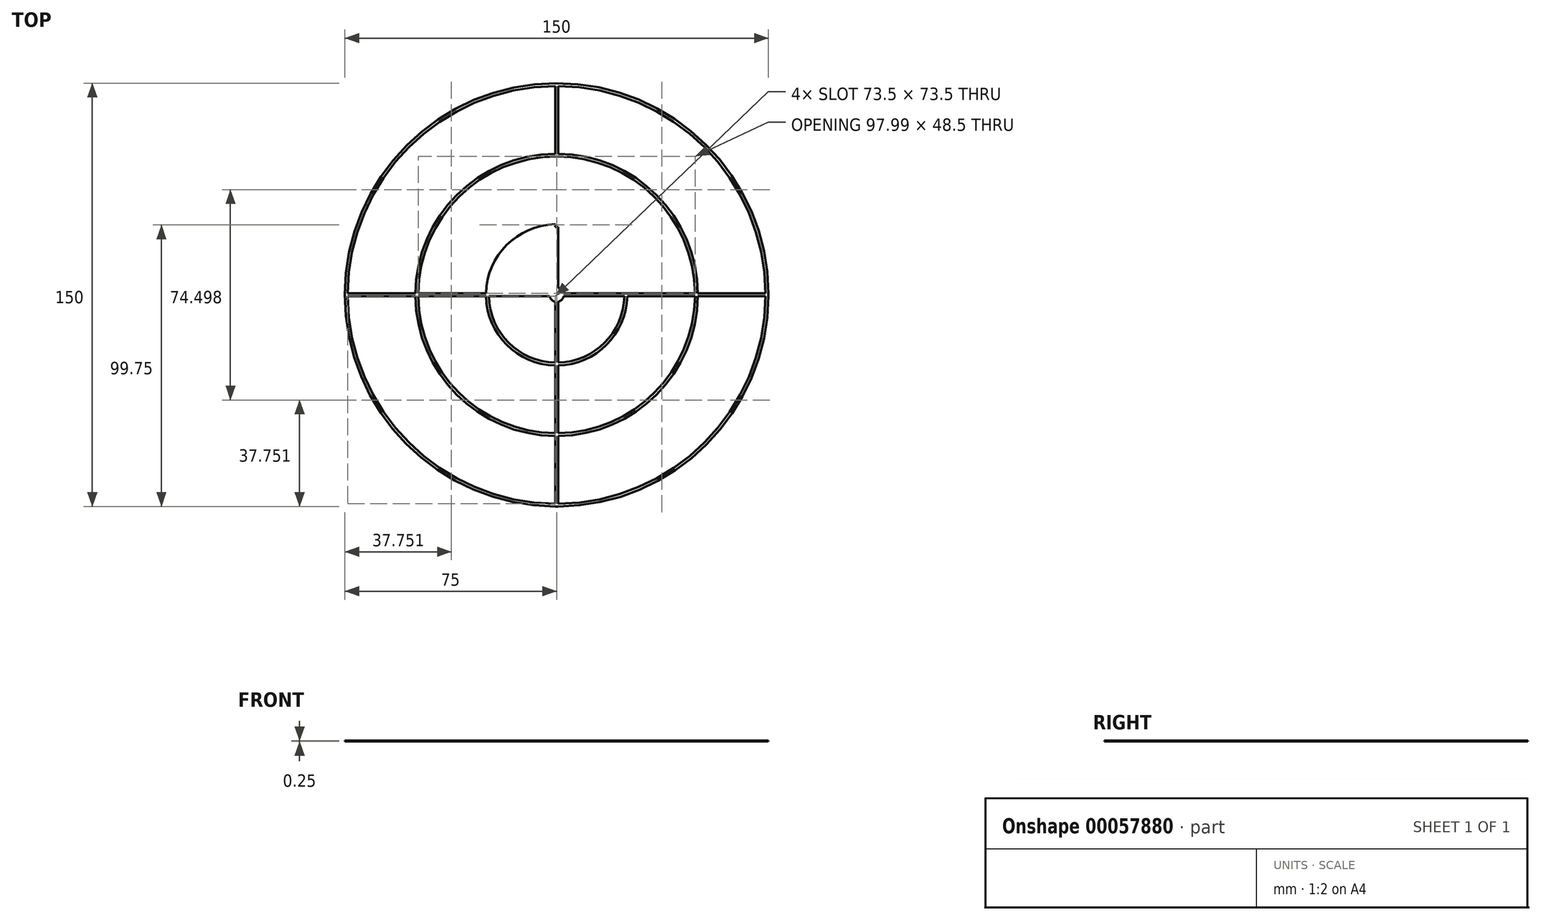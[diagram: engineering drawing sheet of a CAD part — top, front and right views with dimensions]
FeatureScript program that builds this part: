
annotation { "Feature Type Name" : "Feature", "Feature Type Description" : "" }
export const myFeature = defineFeature(function(context is Context, id is Id, definition is map)
    precondition{}
    {
        {
            var Q0;
            Q0=qCreatedBy(makeId("Top.planeOp"),FACE);
            var sketch = newSketch(context, id + "F0", { "sketchPlane" : qUnion([Q0])});
            skArc(sketch, "E0", {"start": v(-74, -0.5) * mm, "mid": v(74, 0) * mm, "end": v(-74, 0.5) * mm});
            skCircle(sketch, "E1", {"center": v(0, 0) * mm, "radius": 75 * mm});
            skLineSegment(sketch, "E2.rect.bottom", {"start": v(0.5, -75) * mm, "end": v(-0.5, -75) * mm});
            skLineSegment(sketch, "E2.rect.top", {"start": v(0.5, 75) * mm, "end": v(-0.5, 75) * mm});
            skLineSegment(sketch, "E2.rect.left", {"start": v(0.5, -75) * mm, "end": v(0.5, -0.5) * mm});
            skLineSegment(sketch, "E2.rect.right", {"start": v(-0.5, -75) * mm, "end": v(-0.5, -50) * mm});
            skLineSegment(sketch, "E3.rect.bottom", {"start": v(75, -0.5) * mm, "end": v(0.5, -0.5) * mm});
            skLineSegment(sketch, "E3.rect.top", {"start": v(75, 0.5) * mm, "end": v(-24, 0.5) * mm});
            skLineSegment(sketch, "E3.rect.left", {"start": v(75, -0.5) * mm, "end": v(75, 0.5) * mm});
            skLineSegment(sketch, "E3.rect.right", {"start": v(-75, -0.5) * mm, "end": v(-75, 0.5) * mm});
            skArc(sketch, "E4", {"start": v(-25, -0.5) * mm, "mid": v(-17.68, -17.68) * mm, "end": v(-0.5, -25) * mm});
            skArc(sketch, "E5", {"start": v(0.5, -24) * mm, "mid": v(16.97, -16.97) * mm, "end": v(24, -0.5) * mm});
            skArc(sketch, "E6", {"start": v(49, -0.5) * mm, "mid": v(0, 49) * mm, "end": v(-49, -0.5) * mm});
            skArc(sketch, "E7", {"start": v(-50, -0.5) * mm, "mid": v(50, 0) * mm, "end": v(-50, 0.5) * mm});
            skArc(sketch, "E8", {"start": v(0.5, -2.45) * mm, "mid": v(1.77, -1.77) * mm, "end": v(2.45, -0.5) * mm});
            skLineSegment(sketch, "E9.trimOffspring", {"start": v(-50, 0.5) * mm, "end": v(-74, 0.5) * mm});
            skLineSegment(sketch, "E10.trimOffspring", {"start": v(-25, 0.5) * mm, "end": v(-49, 0.5) * mm});
            skLineSegment(sketch, "E11.trimOffspring", {"start": v(0.5, 25) * mm, "end": v(0.5, 75) * mm});
            skArc(sketch, "E12.trimOffspring", {"start": v(-0.5, 25) * mm, "mid": v(-17.68, 17.68) * mm, "end": v(-25, 0.5) * mm});
            skLineSegment(sketch, "E13.trimOffspring", {"start": v(-0.5, -49) * mm, "end": v(-0.5, -25) * mm});
            skArc(sketch, "E14.trimOffspring", {"start": v(0.5, -25) * mm, "mid": v(25, 0) * mm, "end": v(0.5, 25) * mm});
            skLineSegment(sketch, "E15.trimOffspring", {"start": v(-0.5, -24) * mm, "end": v(-0.5, 75) * mm});
            skLineSegment(sketch, "E16.trimOffspring", {"start": v(-0.5, -0.5) * mm, "end": v(-74, -0.5) * mm});
            skArc(sketch, "E17.trimOffspring", {"start": v(24, 0.5) * mm, "mid": v(-16.97, 16.97) * mm, "end": v(-0.5, -24) * mm});
            skArc(sketch, "E18.trimOffspring", {"start": v(2.45, 0.5) * mm, "mid": v(1.77, 1.77) * mm, "end": v(0.5, 2.45) * mm});
            skArc(sketch, "E19.trimOffspring", {"start": v(-0.5, 2.45) * mm, "mid": v(-1.77, 1.77) * mm, "end": v(-2.45, 0.5) * mm});
            skArc(sketch, "E20.trimOffspring", {"start": v(-2.45, -0.5) * mm, "mid": v(-1.77, -1.77) * mm, "end": v(-0.5, -2.45) * mm});
            skLineSegment(sketch, "E21.trimOffspring", {"start": v(0.5, 0.5) * mm, "end": v(0.5, 24) * mm});
            skArc(sketch, "E22", {"start": v(-49, -0.5) * mm, "mid": v(0, -49) * mm, "end": v(49, -0.5) * mm});
            skSolve(sketch);
        }
        {
            var Q0;
            {var subQ0=sQuery(id+"F0.wireOp",EDGE,"E2.rect.right");var subQ1=sQuery(id+"F0.wireOp",EDGE,"E0");var subQ2=makeQuery(id+"F0.imprint","INTERSECT",VERTEX,{"derivedFrom":[subQ1,subQ0]});Q0=makeQuery(id+"F0.imprint","IMPRINT",FACE,{"disambiguationData":[TD([[makeQuery(id+"F0.imprint","IMPRINT",EDGE,{"disambiguationData":[TD([[subQ2,-1.0]])],"derivedFrom":subQ1}),1.0]])]});}
            var Q1;
            {var subQ0=sQuery(id+"F0.wireOp",EDGE,"E3.rect.bottom");var subQ1=sQuery(id+"F0.wireOp",EDGE,"E0");var subQ2=makeQuery(id+"F0.imprint","INTERSECT",VERTEX,{"derivedFrom":[subQ1,subQ0]});Q1=makeQuery(id+"F0.imprint","IMPRINT",FACE,{"disambiguationData":[TD([[makeQuery(id+"F0.imprint","IMPRINT",EDGE,{"disambiguationData":[TD([[subQ2,-1.0]])],"derivedFrom":subQ1}),1.0]])]});}
            var Q2;
            {var subQ0=sQuery(id+"F0.wireOp",EDGE,"E11.trimOffspring");var subQ1=sQuery(id+"F0.wireOp",EDGE,"E0");var subQ2=makeQuery(id+"F0.imprint","INTERSECT",VERTEX,{"derivedFrom":[subQ1,subQ0]});Q2=makeQuery(id+"F0.imprint","IMPRINT",FACE,{"disambiguationData":[TD([[makeQuery(id+"F0.imprint","IMPRINT",EDGE,{"disambiguationData":[TD([[subQ2,-1.0]])],"derivedFrom":subQ1}),1.0]])]});}
            var Q3;
            {var subQ0=sQuery(id+"F0.wireOp",EDGE,"E2.rect.right");var subQ1=sQuery(id+"F0.wireOp",EDGE,"E0");var subQ2=makeQuery(id+"F0.imprint","INTERSECT",VERTEX,{"derivedFrom":[subQ1,subQ0]});Q3=makeQuery(id+"F0.imprint","IMPRINT",FACE,{"disambiguationData":[TD([[makeQuery(id+"F0.imprint","IMPRINT",EDGE,{"disambiguationData":[TD([[subQ2,-1.0]])],"derivedFrom":subQ1}),1.0]])]});}
            var Q4;
            {var subQ0=sQuery(id+"F0.wireOp",EDGE,"E3.rect.bottom");var subQ1=sQuery(id+"F0.wireOp",EDGE,"E0");var subQ2=makeQuery(id+"F0.imprint","INTERSECT",VERTEX,{"derivedFrom":[subQ1,subQ0]});Q4=makeQuery(id+"F0.imprint","IMPRINT",FACE,{"disambiguationData":[TD([[makeQuery(id+"F0.imprint","IMPRINT",EDGE,{"disambiguationData":[TD([[subQ2,-1.0]])],"derivedFrom":subQ1}),1.0]])]});}
            var Q5;
            {var subQ0=sQuery(id+"F0.wireOp",EDGE,"E11.trimOffspring");var subQ1=sQuery(id+"F0.wireOp",EDGE,"E0");var subQ2=makeQuery(id+"F0.imprint","INTERSECT",VERTEX,{"derivedFrom":[subQ1,subQ0]});Q5=makeQuery(id+"F0.imprint","IMPRINT",FACE,{"disambiguationData":[TD([[makeQuery(id+"F0.imprint","IMPRINT",EDGE,{"disambiguationData":[TD([[subQ2,-1.0]])],"derivedFrom":subQ1}),1.0]])]});}
            var Q6;
            {var subQ11=sQuery(id+"F0.wireOp",EDGE,"E3.rect.right");Q6=makeQuery(id+"F0.imprint","IMPRINT",FACE,{"disambiguationData":[TD([[makeQuery(id+"F0.imprint","IMPRINT",EDGE,{"derivedFrom":subQ11}),-1.0]])]});}
            var Q7;
            {var subQ0=sQuery(id+"F0.wireOp",EDGE,"E2.rect.top");Q7=makeQuery(id+"F0.imprint","IMPRINT",FACE,{"disambiguationData":[TD([[makeQuery(id+"F0.imprint","IMPRINT",EDGE,{"derivedFrom":subQ0}),-1.0]])]});}
            var Q8;
            {var subQ0=sQuery(id+"F0.wireOp",EDGE,"E3.rect.right");Q8=makeQuery(id+"F0.imprint","IMPRINT",FACE,{"disambiguationData":[TD([[makeQuery(id+"F0.imprint","IMPRINT",EDGE,{"derivedFrom":subQ0}),1.0]])]});}
            var Q9;
            {var subQ3=sQuery(id+"F0.wireOp",EDGE,"E20.trimOffspring");Q9=makeQuery(id+"F0.imprint","IMPRINT",FACE,{"disambiguationData":[TD([[makeQuery(id+"F0.imprint","IMPRINT",EDGE,{"derivedFrom":subQ3}),1.0]])]});}
            var Q10;
            {var subQ0=sQuery(id+"F0.wireOp",EDGE,"E19.trimOffspring");Q10=makeQuery(id+"F0.imprint","IMPRINT",FACE,{"disambiguationData":[TD([[makeQuery(id+"F0.imprint","IMPRINT",EDGE,{"derivedFrom":subQ0}),1.0]])]});}
            var Q11;
            {var subQ0=sQuery(id+"F0.wireOp",EDGE,"E18.trimOffspring");Q11=makeQuery(id+"F0.imprint","IMPRINT",FACE,{"disambiguationData":[TD([[makeQuery(id+"F0.imprint","IMPRINT",EDGE,{"derivedFrom":subQ0}),1.0]])]});}
            var Q12;
            {var subQ3=sQuery(id+"F0.wireOp",EDGE,"E8");Q12=makeQuery(id+"F0.imprint","IMPRINT",FACE,{"disambiguationData":[TD([[makeQuery(id+"F0.imprint","IMPRINT",EDGE,{"derivedFrom":subQ3}),1.0]])]});}
            var Q13;
            {var subQ4=sQuery(id+"F0.wireOp",EDGE,"E3.rect.top");var subQ8=makeQuery(id+"F0.imprint","INTERSECT",VERTEX,{"derivedFrom":[subQ4,sQuery(id+"F0.wireOp",EDGE,"E19.trimOffspring")]});Q13=makeQuery(id+"F0.imprint","IMPRINT",FACE,{"disambiguationData":[TD([[makeQuery(id+"F0.imprint","IMPRINT",EDGE,{"disambiguationData":[TD([[subQ8,1.0]])],"derivedFrom":subQ4}),1.0]])]});}
            var Q14;
            {var subQ22=sQuery(id+"F0.wireOp",EDGE,"E4");Q14=makeQuery(id+"F0.imprint","IMPRINT",FACE,{"disambiguationData":[TD([[makeQuery(id+"F0.imprint","IMPRINT",EDGE,{"derivedFrom":subQ22}),1.0]])]});}
            var Q15;
            {var subQ0=sQuery(id+"F0.wireOp",EDGE,"E5");Q15=makeQuery(id+"F0.imprint","IMPRINT",FACE,{"disambiguationData":[TD([[makeQuery(id+"F0.imprint","IMPRINT",EDGE,{"derivedFrom":subQ0}),-1.0]])]});}
            var Q16;
            {var subQ3=sQuery(id+"F0.wireOp",EDGE,"E3.rect.top");var subQ7=sQuery(id+"F0.wireOp",EDGE,"E17.trimOffspring");var subQ8=makeQuery(id+"F0.imprint","INTERSECT",VERTEX,{"disambiguationData":[OD(1.0)],"derivedFrom":[subQ3,subQ7]});Q16=makeQuery(id+"F0.imprint","IMPRINT",FACE,{"disambiguationData":[TD([[makeQuery(id+"F0.imprint","IMPRINT",EDGE,{"disambiguationData":[TD([[subQ8,1.0]])],"derivedFrom":subQ3}),-1.0]])]});}
            var Q17;
            {var subQ0=sQuery(id+"F0.wireOp",EDGE,"E21.trimOffspring");var subQ6=sQuery(id+"F0.wireOp",EDGE,"E3.rect.top");var subQ7=makeQuery(id+"F0.imprint","INTERSECT",VERTEX,{"derivedFrom":[subQ6,subQ0]});Q17=makeQuery(id+"F0.imprint","IMPRINT",FACE,{"disambiguationData":[TD([[makeQuery(id+"F0.imprint","IMPRINT",EDGE,{"disambiguationData":[TD([[subQ7,-1.0]])],"derivedFrom":subQ6}),-1.0]])]});}
            var Q18;
            {var subQ22=sQuery(id+"F0.wireOp",EDGE,"E4");Q18=makeQuery(id+"F0.imprint","IMPRINT",FACE,{"disambiguationData":[TD([[makeQuery(id+"F0.imprint","IMPRINT",EDGE,{"derivedFrom":subQ22}),1.0]])]});}
            var Q19;
            {var subQ7=sQuery(id+"F0.wireOp",EDGE,"E10.trimOffspring");Q19=makeQuery(id+"F0.imprint","IMPRINT",FACE,{"disambiguationData":[TD([[makeQuery(id+"F0.imprint","IMPRINT",EDGE,{"derivedFrom":subQ7}),1.0]])]});}
            var Q20;
            {var subQ0=sQuery(id+"F0.wireOp",EDGE,"E6");var subQ5=sQuery(id+"F0.wireOp",EDGE,"E3.rect.top");var subQ6=makeQuery(id+"F0.imprint","INTERSECT",VERTEX,{"derivedFrom":[subQ5,subQ0]});Q20=makeQuery(id+"F0.imprint","IMPRINT",FACE,{"disambiguationData":[TD([[makeQuery(id+"F0.imprint","IMPRINT",EDGE,{"disambiguationData":[TD([[subQ6,-1.0]])],"derivedFrom":subQ5}),1.0]])]});}
            var Q21;
            {var subQ3=sQuery(id+"F0.wireOp",EDGE,"E7");var subQ5=sQuery(id+"F0.wireOp",EDGE,"E3.rect.top");var subQ6=makeQuery(id+"F0.imprint","INTERSECT",VERTEX,{"derivedFrom":[subQ5,subQ3]});Q21=makeQuery(id+"F0.imprint","IMPRINT",FACE,{"disambiguationData":[TD([[makeQuery(id+"F0.imprint","IMPRINT",EDGE,{"disambiguationData":[TD([[subQ6,-1.0]])],"derivedFrom":subQ5}),1.0]])]});}
            var Q22;
            {var subQ0=sQuery(id+"F0.wireOp",EDGE,"E7");var subQ1=sQuery(id+"F0.wireOp",EDGE,"E3.rect.top");var subQ2=makeQuery(id+"F0.imprint","INTERSECT",VERTEX,{"derivedFrom":[subQ1,subQ0]});Q22=makeQuery(id+"F0.imprint","IMPRINT",FACE,{"disambiguationData":[TD([[makeQuery(id+"F0.imprint","IMPRINT",EDGE,{"disambiguationData":[TD([[subQ2,-1.0]])],"derivedFrom":subQ1}),-1.0]])]});}
            var Q23;
            {var subQ0=sQuery(id+"F0.wireOp",EDGE,"E7");var subQ1=sQuery(id+"F0.wireOp",EDGE,"E2.rect.left");var subQ2=makeQuery(id+"F0.imprint","INTERSECT",VERTEX,{"derivedFrom":[subQ1,subQ0]});Q23=makeQuery(id+"F0.imprint","IMPRINT",FACE,{"disambiguationData":[TD([[makeQuery(id+"F0.imprint","IMPRINT",EDGE,{"disambiguationData":[TD([[subQ2,-1.0]])],"derivedFrom":subQ1}),-1.0]])]});}
            var Q24;
            {var subQ0=sQuery(id+"F0.wireOp",EDGE,"E3.rect.top");var subQ1=sQuery(id+"F0.wireOp",EDGE,"E0");var subQ2=makeQuery(id+"F0.imprint","INTERSECT",VERTEX,{"derivedFrom":[subQ1,subQ0]});Q24=makeQuery(id+"F0.imprint","IMPRINT",FACE,{"disambiguationData":[TD([[makeQuery(id+"F0.imprint","IMPRINT",EDGE,{"disambiguationData":[TD([[subQ2,-1.0]])],"derivedFrom":subQ1}),-1.0]])]});}
            var Q25;
            {var subQ0=sQuery(id+"F0.wireOp",EDGE,"E2.rect.left");var subQ1=sQuery(id+"F0.wireOp",EDGE,"E0");var subQ2=makeQuery(id+"F0.imprint","INTERSECT",VERTEX,{"derivedFrom":[subQ1,subQ0]});Q25=makeQuery(id+"F0.imprint","IMPRINT",FACE,{"disambiguationData":[TD([[makeQuery(id+"F0.imprint","IMPRINT",EDGE,{"disambiguationData":[TD([[subQ2,-1.0]])],"derivedFrom":subQ1}),-1.0]])]});}
            var Q26;
            {var subQ5=sQuery(id+"F0.wireOp",EDGE,"E3.rect.left");Q26=makeQuery(id+"F0.imprint","IMPRINT",FACE,{"disambiguationData":[TD([[makeQuery(id+"F0.imprint","IMPRINT",EDGE,{"derivedFrom":subQ5}),1.0]])]});}
            var Q27;
            {var subQ3=sQuery(id+"F0.wireOp",EDGE,"E7");var subQ6=sQuery(id+"F0.wireOp",EDGE,"E2.rect.left");var subQ7=makeQuery(id+"F0.imprint","INTERSECT",VERTEX,{"derivedFrom":[subQ6,subQ3]});Q27=makeQuery(id+"F0.imprint","IMPRINT",FACE,{"disambiguationData":[TD([[makeQuery(id+"F0.imprint","IMPRINT",EDGE,{"disambiguationData":[TD([[subQ7,-1.0]])],"derivedFrom":subQ6}),1.0]])]});}
            var Q28;
            {var subQ5=sQuery(id+"F0.wireOp",EDGE,"E2.rect.bottom");Q28=makeQuery(id+"F0.imprint","IMPRINT",FACE,{"disambiguationData":[TD([[makeQuery(id+"F0.imprint","IMPRINT",EDGE,{"derivedFrom":subQ5}),-1.0]])]});}
            var Q29;
            {var subQ0=sQuery(id+"F0.wireOp",EDGE,"E11.trimOffspring");var subQ1=sQuery(id+"F0.wireOp",EDGE,"E6");var subQ2=makeQuery(id+"F0.imprint","INTERSECT",VERTEX,{"derivedFrom":[subQ1,subQ0]});Q29=makeQuery(id+"F0.imprint","IMPRINT",FACE,{"disambiguationData":[TD([[makeQuery(id+"F0.imprint","IMPRINT",EDGE,{"disambiguationData":[TD([[subQ2,-1.0]])],"derivedFrom":subQ1}),-1.0]])]});}
            var Q30;
            {var subQ5=sQuery(id+"F0.wireOp",EDGE,"E2.rect.top");Q30=makeQuery(id+"F0.imprint","IMPRINT",FACE,{"disambiguationData":[TD([[makeQuery(id+"F0.imprint","IMPRINT",EDGE,{"derivedFrom":subQ5}),1.0]])]});}
            extrude(context, id + "F1", {"entities" : qUnion([Q0, Q1, Q2, Q3, Q4, Q5, Q6, Q7, Q8, Q9, Q10, Q11, Q12, Q13, Q14, Q15, Q16, Q17, Q18, Q19, Q20, Q21, Q22, Q23, Q24, Q25, Q26, Q27, Q28, Q29, Q30]), "depth" : .25 * mm});
        }
    });
